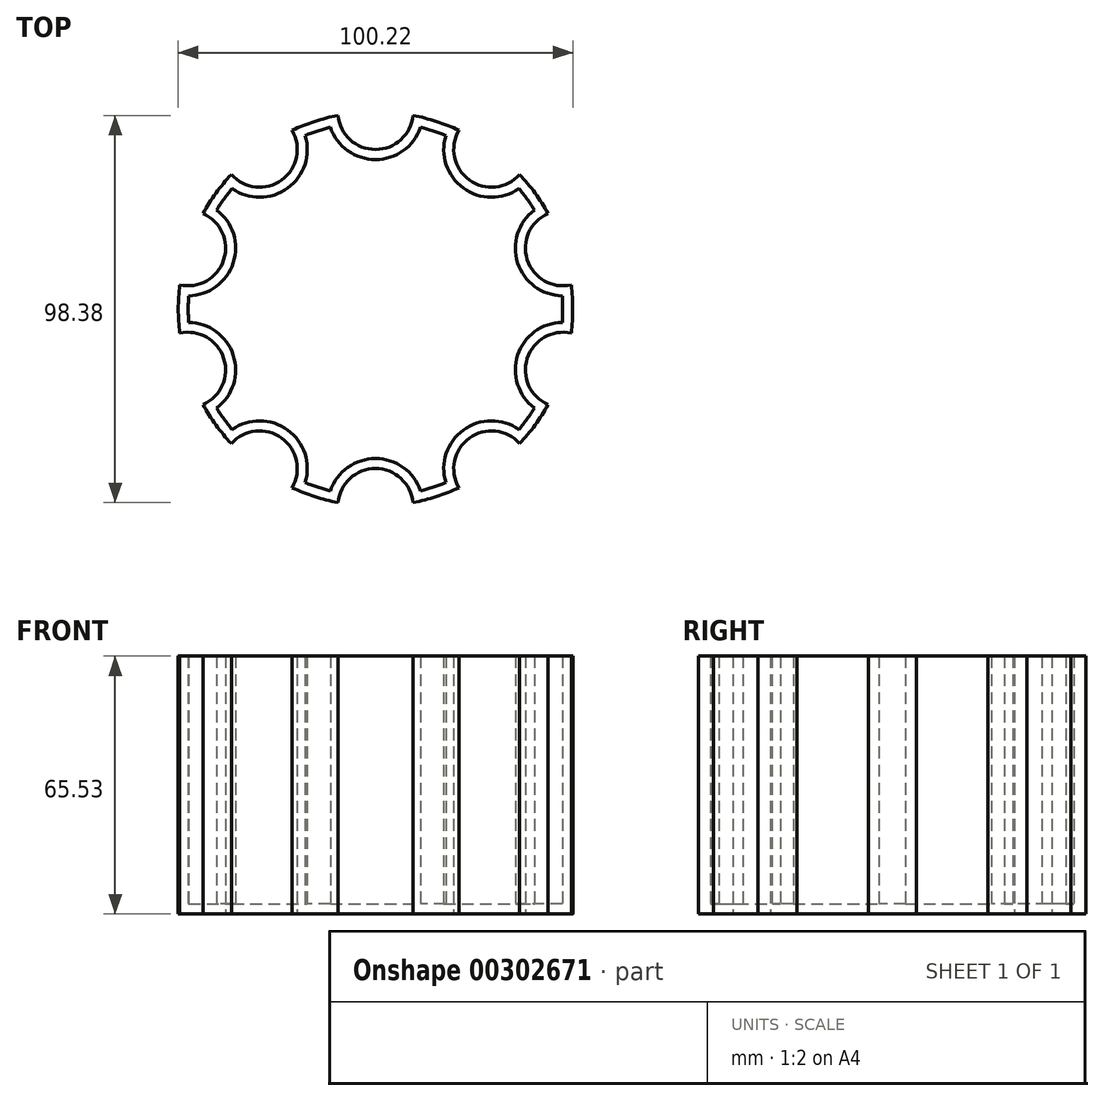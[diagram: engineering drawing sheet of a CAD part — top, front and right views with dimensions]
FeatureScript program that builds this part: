
annotation { "Feature Type Name" : "Feature", "Feature Type Description" : "" }
export const myFeature = defineFeature(function(context is Context, id is Id, definition is map)
    precondition{}
    {
        {
            var Q0;
            Q0=qCreatedBy(makeId("Top.planeOp"),FACE);
            var sketch = newSketch(context, id + "F0", { "sketchPlane" : qUnion([Q0])});
            skCircle(sketch, "E0", {"center": v(0, 0) * mm, "radius": 50.1 * mm});
            skCircle(sketch, "E1", {"center": v(0, 50.1) * mm, "radius": 9.58 * mm});
            skCircle(sketch, "E2.1.1", {"center": v(-29.45, 40.54) * mm, "radius": 9.58 * mm});
            skCircle(sketch, "E2.2.1", {"center": v(-47.66, 15.48) * mm, "radius": 9.58 * mm});
            skCircle(sketch, "E2.3.1", {"center": v(-47.66, -15.48) * mm, "radius": 9.58 * mm});
            skCircle(sketch, "E2.4.1", {"center": v(-29.45, -40.54) * mm, "radius": 9.58 * mm});
            skCircle(sketch, "E2.5.1", {"center": v(0, -50.1) * mm, "radius": 9.58 * mm});
            skCircle(sketch, "E2.6.1", {"center": v(29.45, -40.54) * mm, "radius": 9.58 * mm});
            skCircle(sketch, "E2.7.1", {"center": v(47.66, -15.48) * mm, "radius": 9.58 * mm});
            skCircle(sketch, "E2.8.1", {"center": v(47.66, 15.48) * mm, "radius": 9.58 * mm});
            skCircle(sketch, "E2.9.1", {"center": v(29.45, 40.54) * mm, "radius": 9.58 * mm});
            skSolve(sketch);
        }
        {
            var Q0;
            {var subQ0=sQuery(id+"F0.wireOp",EDGE,"E0");var subQ18=sQuery(id+"F0.wireOp",EDGE,"E1");var subQ19=makeQuery(id+"F0.imprint","INTERSECT",VERTEX,{"disambiguationData":[OD(0.0)],"derivedFrom":[subQ18,subQ0]});Q0=makeQuery(id+"F0.imprint","IMPRINT",FACE,{"disambiguationData":[TD([[makeQuery(id+"F0.imprint","IMPRINT",EDGE,{"disambiguationData":[TD([[subQ19,1.0]])],"derivedFrom":subQ18}),-1.0]])]});}
            extrude(context, id + "F1", {"entities" : qUnion([Q0]), "depth" : 65.53 * mm});
        }
        {
            var Q0;
            Q0=makeQuery(id+"F1.opExtrude","CAP_FACE",FACE,{"disambiguationData":[OSD([sQuery(id+"F0.wireOp",EDGE,"E1"),sQuery(id+"F0.wireOp",EDGE,"E2.1.1"),sQuery(id+"F0.wireOp",EDGE,"E2.2.1"),sQuery(id+"F0.wireOp",EDGE,"E2.3.1"),sQuery(id+"F0.wireOp",EDGE,"E2.4.1"),sQuery(id+"F0.wireOp",EDGE,"E2.5.1"),sQuery(id+"F0.wireOp",EDGE,"E2.6.1"),sQuery(id+"F0.wireOp",EDGE,"E2.7.1"),sQuery(id+"F0.wireOp",EDGE,"E2.8.1"),sQuery(id+"F0.wireOp",EDGE,"E0"),sQuery(id+"F0.wireOp",EDGE,"E2.9.1")])],"isStart":false});
            shell(context, id + "F2", {"entities" : qUnion([Q0]), "thickness" : 2.54 * mm});
        }
    });
